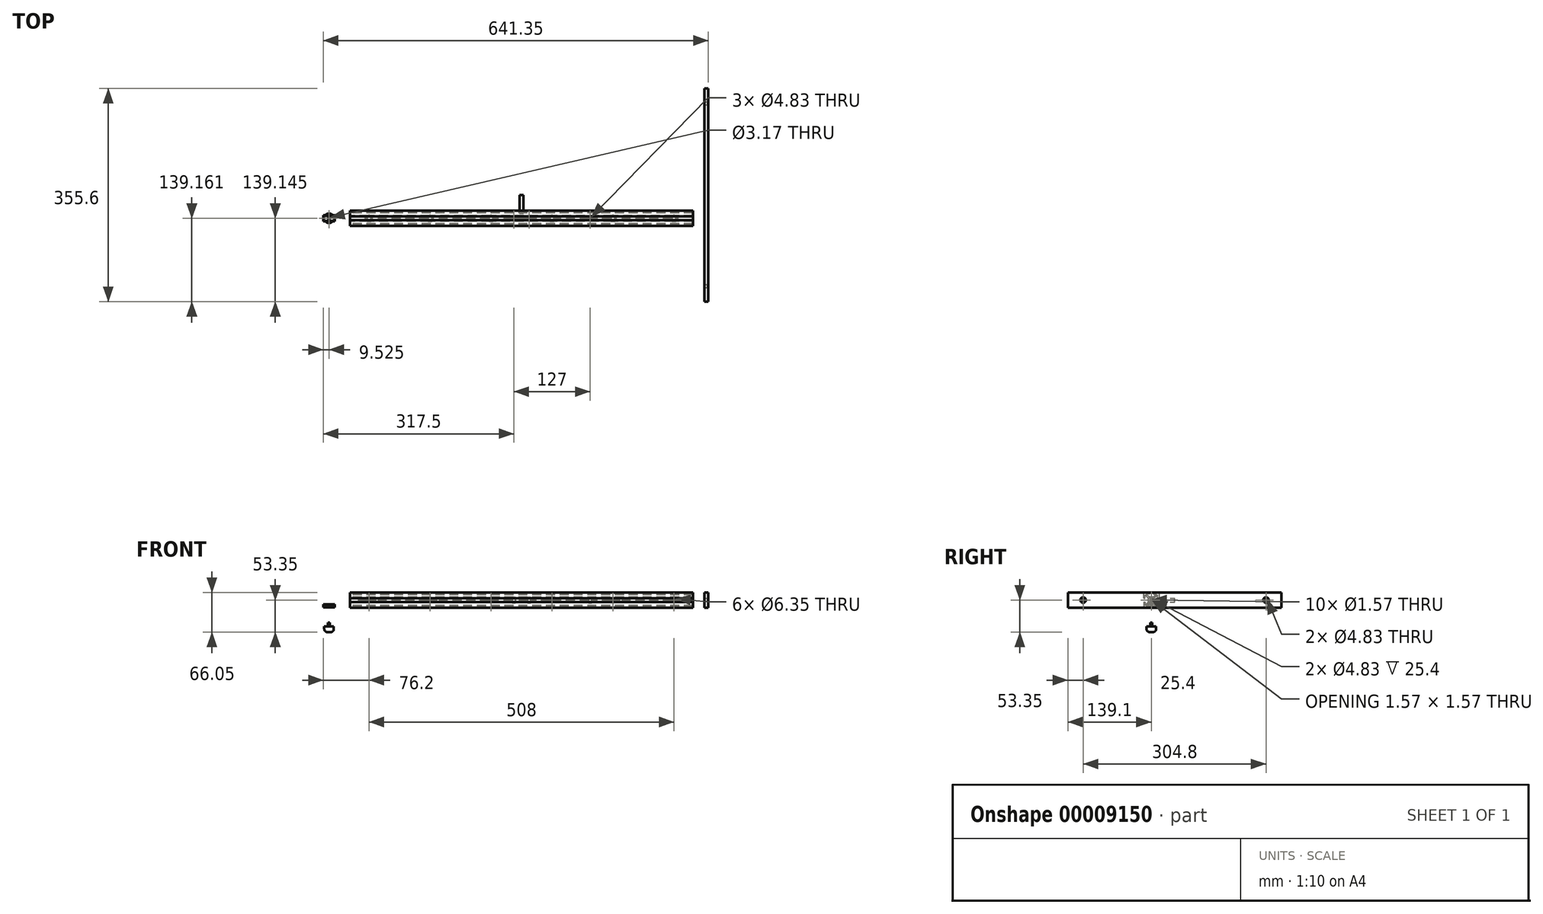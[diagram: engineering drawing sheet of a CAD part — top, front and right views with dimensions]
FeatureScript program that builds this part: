
annotation { "Feature Type Name" : "Feature", "Feature Type Description" : "" }
export const myFeature = defineFeature(function(context is Context, id is Id, definition is map)
    precondition{}
    {
        {
            var Q0;
            Q0=qCreatedBy(makeId("Right.planeOp"),FACE);
            var sketch = newSketch(context, id + "F0", { "sketchPlane" : qUnion([Q0])});
            skLineSegment(sketch, "E0.rect.bottom", {"start": v(-26, -12.7) * mm, "end": v(-35.53, -12.7) * mm});
            skLineSegment(sketch, "E0.rect.left", {"start": v(-26, -12.7) * mm, "end": v(-26, -3.18) * mm});
            skPoint(sketch, "E0.rect.middle", {"position": v(-38.7, 0) * mm});
            skLineSegment(sketch, "E1", {"start": v(-41.88, 12.7) * mm, "end": v(-41.88, 10.34) * mm});
            skLineSegment(sketch, "E2", {"start": v(-51.4, 3.17) * mm, "end": v(-49.04, 3.17) * mm});
            skLineSegment(sketch, "E3.rect.bottom", {"start": v(-35.6, -4.76) * mm, "end": v(-41.79, -4.76) * mm});
            skLineSegment(sketch, "E3.rect.top", {"start": v(-35.6, 4.76) * mm, "end": v(-41.8, 4.76) * mm});
            skLineSegment(sketch, "E3.rect.left", {"start": v(-33.94, -3.1) * mm, "end": v(-33.94, 3.1) * mm});
            skLineSegment(sketch, "E3.rect.right", {"start": v(-43.46, -3.09) * mm, "end": v(-43.46, 3.1) * mm});
            skLineSegment(sketch, "E4", {"start": v(-47.37, 10.34) * mm, "end": v(-41.8, 4.76) * mm});
            skLineSegment(sketch, "E5", {"start": v(-49.04, 8.67) * mm, "end": v(-43.46, 3.1) * mm});
            skLineSegment(sketch, "E6", {"start": v(-41.88, 10.34) * mm, "end": v(-47.37, 10.34) * mm});
            skLineSegment(sketch, "E7", {"start": v(-49.04, 3.17) * mm, "end": v(-49.04, 8.67) * mm});
            skLineSegment(sketch, "E8", {"start": v(-35.53, -12.7) * mm, "end": v(-35.53, -10.34) * mm});
            skLineSegment(sketch, "E9", {"start": v(-26, -3.18) * mm, "end": v(-28.36, -3.18) * mm});
            skLineSegment(sketch, "E10", {"start": v(-35.53, -10.34) * mm, "end": v(-30.03, -10.34) * mm});
            skLineSegment(sketch, "E11", {"start": v(-28.36, -3.18) * mm, "end": v(-28.36, -8.67) * mm});
            skLineSegment(sketch, "E12.trimOffspring", {"start": v(-35.6, -4.76) * mm, "end": v(-30.03, -10.34) * mm});
            skLineSegment(sketch, "E13.trimOffspring", {"start": v(-33.94, -3.1) * mm, "end": v(-28.36, -8.67) * mm});
            skLineSegment(sketch, "E14", {"start": v(-51.4, 12.7) * mm, "end": v(-41.88, 12.7) * mm});
            skLineSegment(sketch, "E15", {"start": v(-51.4, -3.18) * mm, "end": v(-49.04, -3.18) * mm});
            skLineSegment(sketch, "E16", {"start": v(-41.88, -12.7) * mm, "end": v(-41.88, -10.34) * mm});
            skLineSegment(sketch, "E17", {"start": v(-49.04, -3.18) * mm, "end": v(-49.04, -8.66) * mm});
            skLineSegment(sketch, "E18", {"start": v(-41.88, -10.34) * mm, "end": v(-47.36, -10.34) * mm});
            skLineSegment(sketch, "E19", {"start": v(-26, 3.17) * mm, "end": v(-28.36, 3.17) * mm});
            skLineSegment(sketch, "E20", {"start": v(-28.36, 3.17) * mm, "end": v(-28.36, 8.67) * mm});
            skLineSegment(sketch, "E21", {"start": v(-35.53, 12.7) * mm, "end": v(-35.53, 10.34) * mm});
            skLineSegment(sketch, "E22.trimOffspring", {"start": v(-41.88, 12.7) * mm, "end": v(-51.4, 12.7) * mm});
            skLineSegment(sketch, "E23.trimOffspring", {"start": v(-51.4, 3.17) * mm, "end": v(-51.4, 12.7) * mm});
            skLineSegment(sketch, "E24.trimOffspring", {"start": v(-43.46, -3.09) * mm, "end": v(-49.04, -8.66) * mm});
            skLineSegment(sketch, "E25.trimOffspring", {"start": v(-41.79, -4.76) * mm, "end": v(-47.36, -10.34) * mm});
            skLineSegment(sketch, "E26", {"start": v(-35.53, 12.7) * mm, "end": v(-26, 12.7) * mm});
            skLineSegment(sketch, "E27", {"start": v(-26, 12.7) * mm, "end": v(-26, 3.17) * mm});
            skLineSegment(sketch, "E28", {"start": v(-51.4, -3.18) * mm, "end": v(-51.4, -12.7) * mm});
            skLineSegment(sketch, "E29", {"start": v(-51.4, -12.7) * mm, "end": v(-41.88, -12.7) * mm});
            skCircle(sketch, "E30", {"center": v(-38.7, 0) * mm, "radius": 0.79 * mm});
            skLineSegment(sketch, "E31", {"start": v(-35.53, 10.34) * mm, "end": v(-30.03, 10.34) * mm});
            skLineSegment(sketch, "E32", {"start": v(-30.03, 10.34) * mm, "end": v(-35.6, 4.76) * mm});
            skLineSegment(sketch, "E33", {"start": v(-28.36, 8.67) * mm, "end": v(-33.94, 3.1) * mm});
            skSolve(sketch);
        }
        {
            var Q0;
            Q0=makeQuery(id+"F0.imprint","IMPRINT",FACE,{"disambiguationData":[TD([[makeQuery(id+"F0.imprint","IMPRINT",EDGE,{"derivedFrom":sQuery(id+"F0.wireOp",EDGE,"E0.rect.bottom")}),-1.0]])]});
            extrude(context, id + "F1", {"entities" : qUnion([Q0]), "depth" : 285.75 * mm, "hasSecondDirection" : true, "secondDirectionOppositeDirection" : true, "secondDirectionDepth" : 285.75 * mm});
        }
        {
            var Q0;
            Q0=makeQuery(id+"F1.opExtrude","SWEPT_FACE",FACE,{"disambiguationData":[OSD([sQuery(id+"F0.wireOp",EDGE,"E23.trimOffspring")])]});
            cPlane(context, id + "F2", {"entities" : qUnion([Q0]), "cplaneType" : CPlaneType.OFFSET, "offset" : 0 * mm, "width" : 152.4 * mm, "height" : 152.4 * mm});
        }
        {
            var Q0;
            Q0=qCreatedBy(id+"F2.planeOp",FACE);
            var sketch = newSketch(context, id + "F3", { "sketchPlane" : qUnion([Q0])});
            skCircle(sketch, "E34", {"center": v(-50.8, 0) * mm, "radius": 3.18 * mm});
            skCircle(sketch, "E35", {"center": v(50.8, 0) * mm, "radius": 3.18 * mm});
            skCircle(sketch, "E36", {"center": v(152.4, 0) * mm, "radius": 3.18 * mm});
            skCircle(sketch, "E37", {"center": v(254, 0) * mm, "radius": 3.18 * mm});
            skCircle(sketch, "E38", {"center": v(-254, 0) * mm, "radius": 3.18 * mm});
            skCircle(sketch, "E39", {"center": v(-152.4, 0) * mm, "radius": 3.18 * mm});
            skSolve(sketch);
        }
        {
            var Q0;
            Q0=makeQuery(id+"F3.imprint","IMPRINT",FACE,{"disambiguationData":[TD([[makeQuery(id+"F3.imprint","IMPRINT",EDGE,{"derivedFrom":sQuery(id+"F3.wireOp",EDGE,"9be4c3ad-e5e0-4c26-be88-867d9b3b50b8")}),1.0]])]});
            var Q1;
            Q1=makeQuery(id+"F3.imprint","IMPRINT",FACE,{"disambiguationData":[TD([[makeQuery(id+"F3.imprint","IMPRINT",EDGE,{"derivedFrom":sQuery(id+"F3.wireOp",EDGE,"E37")}),1.0]])]});
            var Q2;
            Q2=makeQuery(id+"F3.imprint","IMPRINT",FACE,{"disambiguationData":[TD([[makeQuery(id+"F3.imprint","IMPRINT",EDGE,{"derivedFrom":sQuery(id+"F3.wireOp",EDGE,"E36")}),1.0]])]});
            var Q3;
            Q3=makeQuery(id+"F3.imprint","IMPRINT",FACE,{"disambiguationData":[TD([[makeQuery(id+"F3.imprint","IMPRINT",EDGE,{"derivedFrom":sQuery(id+"F3.wireOp",EDGE,"E35")}),1.0]])]});
            var Q4;
            Q4=makeQuery(id+"F3.imprint","IMPRINT",FACE,{"disambiguationData":[TD([[makeQuery(id+"F3.imprint","IMPRINT",EDGE,{"derivedFrom":sQuery(id+"F3.wireOp",EDGE,"E34")}),1.0]])]});
            var Q5;
            Q5=makeQuery(id+"F3.imprint","IMPRINT",FACE,{"disambiguationData":[TD([[makeQuery(id+"F3.imprint","IMPRINT",EDGE,{"derivedFrom":sQuery(id+"F3.wireOp",EDGE,"E39")}),1.0]])]});
            var Q6;
            Q6=makeQuery(id+"F3.imprint","IMPRINT",FACE,{"disambiguationData":[TD([[makeQuery(id+"F3.imprint","IMPRINT",EDGE,{"derivedFrom":sQuery(id+"F3.wireOp",EDGE,"E38")}),1.0]])]});
            extrude(context, id + "F4", {"entities" : qUnion([Q0, Q1, Q2, Q3, Q4, Q5, Q6]), "operationType" : NewBodyOperationType.REMOVE, "endBound" : BoundingType.THROUGH_ALL, "oppositeDirection" : true, "depth" : 12.7 * mm});
        }
        {
            var Q0;
            Q0=qCreatedBy(makeId("Front.planeOp"),FACE);
            var sketch = newSketch(context, id + "F5", { "sketchPlane" : qUnion([Q0])});
            skCircle(sketch, "E40", {"center": v(0, 0) * mm, "radius": 3.18 * mm});
            skSolve(sketch);
        }
        {
            var Q0;
            Q0=makeQuery(id+"F5.imprint","IMPRINT",FACE,{"disambiguationData":[TD([[makeQuery(id+"F5.imprint","IMPRINT",EDGE,{"derivedFrom":sQuery(id+"F5.wireOp",EDGE,"E40")}),1.0]])]});
            extrude(context, id + "F6", {"entities" : qUnion([Q0]), "depth" : 30.15 * mm});
        }
        {
            var Q0;
            Q0=makeQuery(id+"F1.opExtrude","SWEPT_FACE",FACE,{"disambiguationData":[OSD([sQuery(id+"F0.wireOp",EDGE,"E29")])]});
            cPlane(context, id + "F7", {"entities" : qUnion([Q0]), "cplaneType" : CPlaneType.OFFSET, "offset" : 0 * mm, "width" : 152.4 * mm, "height" : 152.4 * mm});
        }
        {
            var Q0;
            Q0=qCreatedBy(id+"F7.planeOp",FACE);
            var sketch = newSketch(context, id + "F8", { "sketchPlane" : qUnion([Q0])});
            skPoint(sketch, "E41", {"position": v(114.3, 38.65) * mm});
            skLineSegment(sketch, "E42", {"start": v(114.3, 48.26) * mm, "end": v(114.3, 29.05) * mm, "construction": true});
            skCircle(sketch, "E43", {"center": v(114.3, 38.65) * mm, "radius": 2.41 * mm});
            skCircle(sketch, "E44", {"center": v(-12.7, 38.65) * mm, "radius": 2.41 * mm});
            skCircle(sketch, "E45", {"center": v(12.7, 38.65) * mm, "radius": 2.41 * mm});
            skSolve(sketch);
        }
        {
            var Q0;
            Q0=makeQuery(id+"F8.imprint","IMPRINT",FACE,{"disambiguationData":[TD([[makeQuery(id+"F8.imprint","IMPRINT",EDGE,{"derivedFrom":sQuery(id+"F8.wireOp",EDGE,"E43")}),1.0]])]});
            var Q1;
            Q1=makeQuery(id+"F8.imprint","IMPRINT",FACE,{"disambiguationData":[TD([[makeQuery(id+"F8.imprint","IMPRINT",EDGE,{"derivedFrom":sQuery(id+"F8.wireOp",EDGE,"E45")}),1.0]])]});
            var Q2;
            Q2=makeQuery(id+"F8.imprint","IMPRINT",FACE,{"disambiguationData":[TD([[makeQuery(id+"F8.imprint","IMPRINT",EDGE,{"derivedFrom":sQuery(id+"F8.wireOp",EDGE,"E44")}),1.0]])]});
            extrude(context, id + "F9", {"entities" : qUnion([Q0, Q1, Q2]), "operationType" : NewBodyOperationType.REMOVE, "endBound" : BoundingType.THROUGH_ALL, "oppositeDirection" : true, "depth" : 25.4 * mm});
        }
        {
            var Q0;
            Q0=makeQuery(id+"F1.opExtrude","CAP_FACE",FACE,{"disambiguationData":[OSD([sQuery(id+"F0.wireOp",EDGE,"E0.rect.bottom"),sQuery(id+"F0.wireOp",EDGE,"E1"),sQuery(id+"F0.wireOp",EDGE,"E2"),sQuery(id+"F0.wireOp",EDGE,"E3.rect.bottom"),sQuery(id+"F0.wireOp",EDGE,"E3.rect.top"),sQuery(id+"F0.wireOp",EDGE,"E3.rect.left"),sQuery(id+"F0.wireOp",EDGE,"E3.rect.right"),sQuery(id+"F0.wireOp",EDGE,"E4"),sQuery(id+"F0.wireOp",EDGE,"E5"),sQuery(id+"F0.wireOp",EDGE,"E6"),sQuery(id+"F0.wireOp",EDGE,"E7"),sQuery(id+"F0.wireOp",EDGE,"E8"),sQuery(id+"F0.wireOp",EDGE,"E9"),sQuery(id+"F0.wireOp",EDGE,"E10"),sQuery(id+"F0.wireOp",EDGE,"E11"),sQuery(id+"F0.wireOp",EDGE,"E12.trimOffspring"),sQuery(id+"F0.wireOp",EDGE,"E13.trimOffspring"),sQuery(id+"F0.wireOp",EDGE,"E0.rect.left"),sQuery(id+"F0.wireOp",EDGE,"E15"),sQuery(id+"F0.wireOp",EDGE,"E16"),sQuery(id+"F0.wireOp",EDGE,"E17"),sQuery(id+"F0.wireOp",EDGE,"E18"),sQuery(id+"F0.wireOp",EDGE,"E19"),sQuery(id+"F0.wireOp",EDGE,"E20"),sQuery(id+"F0.wireOp",EDGE,"E21"),sQuery(id+"F0.wireOp",EDGE,"E22.trimOffspring"),sQuery(id+"F0.wireOp",EDGE,"E23.trimOffspring"),sQuery(id+"F0.wireOp",EDGE,"E24.trimOffspring"),sQuery(id+"F0.wireOp",EDGE,"E25.trimOffspring"),sQuery(id+"F0.wireOp",EDGE,"E26"),sQuery(id+"F0.wireOp",EDGE,"E27"),sQuery(id+"F0.wireOp",EDGE,"E28"),sQuery(id+"F0.wireOp",EDGE,"E29"),sQuery(id+"F0.wireOp",EDGE,"E30"),sQuery(id+"F0.wireOp",EDGE,"E31"),sQuery(id+"F0.wireOp",EDGE,"E32"),sQuery(id+"F0.wireOp",EDGE,"E33")])],"isStart":false});
            var sketch = newSketch(context, id + "F10", { "sketchPlane" : qUnion([Q0])});
            skCircle(sketch, "E46", {"center": v(-38.7, 0) * mm, "radius": 2.41 * mm});
            skSolve(sketch);
        }
        {
            var Q0;
            Q0=makeQuery(id+"F10.imprint","IMPRINT",FACE,{"disambiguationData":[TD([[makeQuery(id+"F10.imprint","IMPRINT",EDGE,{"derivedFrom":sQuery(id+"F10.wireOp",EDGE,"E46")}),1.0]])]});
            extrude(context, id + "F11", {"entities" : qUnion([Q0]), "operationType" : NewBodyOperationType.REMOVE, "oppositeDirection" : true, "depth" : 25.4 * mm});
        }
        {
            var Q0;
            Q0=makeQuery(id+"F1.opExtrude","CAP_FACE",FACE,{"disambiguationData":[OSD([sQuery(id+"F0.wireOp",EDGE,"E0.rect.bottom"),sQuery(id+"F0.wireOp",EDGE,"E1"),sQuery(id+"F0.wireOp",EDGE,"E2"),sQuery(id+"F0.wireOp",EDGE,"E3.rect.bottom"),sQuery(id+"F0.wireOp",EDGE,"E3.rect.top"),sQuery(id+"F0.wireOp",EDGE,"E3.rect.left"),sQuery(id+"F0.wireOp",EDGE,"E3.rect.right"),sQuery(id+"F0.wireOp",EDGE,"E4"),sQuery(id+"F0.wireOp",EDGE,"E5"),sQuery(id+"F0.wireOp",EDGE,"E6"),sQuery(id+"F0.wireOp",EDGE,"E7"),sQuery(id+"F0.wireOp",EDGE,"E8"),sQuery(id+"F0.wireOp",EDGE,"E9"),sQuery(id+"F0.wireOp",EDGE,"E10"),sQuery(id+"F0.wireOp",EDGE,"E11"),sQuery(id+"F0.wireOp",EDGE,"E12.trimOffspring"),sQuery(id+"F0.wireOp",EDGE,"E13.trimOffspring"),sQuery(id+"F0.wireOp",EDGE,"E0.rect.left"),sQuery(id+"F0.wireOp",EDGE,"E15"),sQuery(id+"F0.wireOp",EDGE,"E16"),sQuery(id+"F0.wireOp",EDGE,"E17"),sQuery(id+"F0.wireOp",EDGE,"E18"),sQuery(id+"F0.wireOp",EDGE,"E19"),sQuery(id+"F0.wireOp",EDGE,"E20"),sQuery(id+"F0.wireOp",EDGE,"E21"),sQuery(id+"F0.wireOp",EDGE,"E22.trimOffspring"),sQuery(id+"F0.wireOp",EDGE,"E23.trimOffspring"),sQuery(id+"F0.wireOp",EDGE,"E24.trimOffspring"),sQuery(id+"F0.wireOp",EDGE,"E25.trimOffspring"),sQuery(id+"F0.wireOp",EDGE,"E26"),sQuery(id+"F0.wireOp",EDGE,"E27"),sQuery(id+"F0.wireOp",EDGE,"E28"),sQuery(id+"F0.wireOp",EDGE,"E29"),sQuery(id+"F0.wireOp",EDGE,"E30"),sQuery(id+"F0.wireOp",EDGE,"E31"),sQuery(id+"F0.wireOp",EDGE,"E32"),sQuery(id+"F0.wireOp",EDGE,"E33")])],"isStart":true});
            var sketch = newSketch(context, id + "F12", { "sketchPlane" : qUnion([Q0])});
            skCircle(sketch, "E47", {"center": v(38.7, 0) * mm, "radius": 2.41 * mm});
            skSolve(sketch);
        }
        {
            var Q0;
            Q0=makeQuery(id+"F12.imprint","IMPRINT",FACE,{"disambiguationData":[TD([[makeQuery(id+"F12.imprint","IMPRINT",EDGE,{"derivedFrom":sQuery(id+"F12.wireOp",EDGE,"E47")}),1.0]])]});
            extrude(context, id + "F13", {"entities" : qUnion([Q0]), "operationType" : NewBodyOperationType.REMOVE, "oppositeDirection" : true, "depth" : 25.4 * mm});
        }
        {
            var Q0;
            Q0=qCreatedBy(makeId("Right.planeOp"),FACE);
            cPlane(context, id + "F14", {"entities" : qUnion([Q0]), "cplaneType" : CPlaneType.OFFSET, "offset" : 304.8 * mm, "width" : 152.4 * mm, "height" : 152.4 * mm});
        }
        {
            var Q0;
            Q0=qCreatedBy(id+"F14.planeOp",FACE);
            var sketch = newSketch(context, id + "F15", { "sketchPlane" : qUnion([Q0])});
            skLineSegment(sketch, "E48.rect.bottom", {"start": v(177.8, -12.7) * mm, "end": v(-177.8, -12.7) * mm});
            skLineSegment(sketch, "E48.rect.top", {"start": v(177.8, 12.7) * mm, "end": v(-177.8, 12.7) * mm});
            skLineSegment(sketch, "E48.rect.left", {"start": v(177.8, -12.7) * mm, "end": v(177.8, 12.7) * mm});
            skLineSegment(sketch, "E48.rect.right", {"start": v(-177.8, -12.7) * mm, "end": v(-177.8, 12.7) * mm});
            skPoint(sketch, "E48.rect.middle", {"position": v(0, 0) * mm});
            skCircle(sketch, "E49", {"center": v(-152.4, 0) * mm, "radius": 2.41 * mm});
            skCircle(sketch, "E50", {"center": v(152.4, 0) * mm, "radius": 2.41 * mm});
            skSolve(sketch);
        }
        {
            var Q0;
            Q0=makeQuery(id+"F15.imprint","IMPRINT",FACE,{"disambiguationData":[TD([[makeQuery(id+"F15.imprint","IMPRINT",EDGE,{"derivedFrom":sQuery(id+"F15.wireOp",EDGE,"E48.rect.bottom")}),-1.0]])]});
            extrude(context, id + "F16", {"entities" : qUnion([Q0]), "depth" : 6.35 * mm});
        }
        {
            var Q0;
            Q0=makeQuery(id+"F16.opExtrude","CAP_EDGE",EDGE,{"disambiguationData":[OSD([sQuery(id+"F15.wireOp",EDGE,"E49")])],"isStart":false});
            var Q1;
            Q1=makeQuery(id+"F16.opExtrude","CAP_EDGE",EDGE,{"disambiguationData":[OSD([sQuery(id+"F15.wireOp",EDGE,"E50")])],"isStart":false});
            chamfer(context, id + "F17", {"entities" : qUnion([Q0, Q1]), "chamferType" : ChamferType.OFFSET_ANGLE, "width" : 1.27 * mm, "oppositeDirection" : false, "angle" : 60 * degree, "tangentPropagation" : true});
        }
        {
            var Q0;
            Q0=makeQuery(id+"F1.opExtrude","CAP_FACE",FACE,{"disambiguationData":[OSD([sQuery(id+"F0.wireOp",EDGE,"E0.rect.bottom"),sQuery(id+"F0.wireOp",EDGE,"E1"),sQuery(id+"F0.wireOp",EDGE,"E2"),sQuery(id+"F0.wireOp",EDGE,"E3.rect.bottom"),sQuery(id+"F0.wireOp",EDGE,"E3.rect.top"),sQuery(id+"F0.wireOp",EDGE,"E3.rect.left"),sQuery(id+"F0.wireOp",EDGE,"E3.rect.right"),sQuery(id+"F0.wireOp",EDGE,"E4"),sQuery(id+"F0.wireOp",EDGE,"E5"),sQuery(id+"F0.wireOp",EDGE,"E6"),sQuery(id+"F0.wireOp",EDGE,"E7"),sQuery(id+"F0.wireOp",EDGE,"E8"),sQuery(id+"F0.wireOp",EDGE,"E9"),sQuery(id+"F0.wireOp",EDGE,"E10"),sQuery(id+"F0.wireOp",EDGE,"E11"),sQuery(id+"F0.wireOp",EDGE,"E12.trimOffspring"),sQuery(id+"F0.wireOp",EDGE,"E13.trimOffspring"),sQuery(id+"F0.wireOp",EDGE,"E0.rect.left"),sQuery(id+"F0.wireOp",EDGE,"E15"),sQuery(id+"F0.wireOp",EDGE,"E16"),sQuery(id+"F0.wireOp",EDGE,"E17"),sQuery(id+"F0.wireOp",EDGE,"E18"),sQuery(id+"F0.wireOp",EDGE,"E19"),sQuery(id+"F0.wireOp",EDGE,"E20"),sQuery(id+"F0.wireOp",EDGE,"E21"),sQuery(id+"F0.wireOp",EDGE,"E22.trimOffspring"),sQuery(id+"F0.wireOp",EDGE,"E23.trimOffspring"),sQuery(id+"F0.wireOp",EDGE,"E24.trimOffspring"),sQuery(id+"F0.wireOp",EDGE,"E25.trimOffspring"),sQuery(id+"F0.wireOp",EDGE,"E26"),sQuery(id+"F0.wireOp",EDGE,"E27"),sQuery(id+"F0.wireOp",EDGE,"E28"),sQuery(id+"F0.wireOp",EDGE,"E29"),sQuery(id+"F0.wireOp",EDGE,"E30"),sQuery(id+"F0.wireOp",EDGE,"E31"),sQuery(id+"F0.wireOp",EDGE,"E32"),sQuery(id+"F0.wireOp",EDGE,"E33")])],"isStart":true});
            cPlane(context, id + "F18", {"entities" : qUnion([Q0]), "cplaneType" : CPlaneType.OFFSET, "offset" : 25.4 * mm, "width" : 152.4 * mm, "height" : 152.4 * mm});
        }
        {
            var Q0;
            Q0=qCreatedBy(id+"F18.planeOp",FACE);
            var sketch = newSketch(context, id + "F19", { "sketchPlane" : qUnion([Q0])});
            skLineSegment(sketch, "E51.bottom", {"start": v(33.56, -7) * mm, "end": v(43.72, -7) * mm});
            skLineSegment(sketch, "E51.top", {"start": v(33.56, -10.17) * mm, "end": v(35.46, -10.17) * mm});
            skLineSegment(sketch, "E51.left", {"start": v(33.56, -7) * mm, "end": v(33.56, -10.17) * mm});
            skLineSegment(sketch, "E51.right", {"start": v(43.72, -7) * mm, "end": v(43.72, -10.17) * mm});
            skLineSegment(sketch, "E52", {"start": v(35.46, -10.17) * mm, "end": v(35.46, -12.07) * mm});
            skLineSegment(sketch, "E53", {"start": v(35.46, -12.07) * mm, "end": v(41.81, -12.07) * mm});
            skLineSegment(sketch, "E54", {"start": v(41.81, -12.07) * mm, "end": v(41.81, -10.17) * mm});
            skLineSegment(sketch, "E55.trimOffspring", {"start": v(41.81, -10.17) * mm, "end": v(43.72, -10.17) * mm});
            skSolve(sketch);
        }
        {
            var Q0;
            Q0=makeQuery(id+"F19.imprint","IMPRINT",FACE,{"disambiguationData":[TD([[makeQuery(id+"F19.imprint","IMPRINT",EDGE,{"derivedFrom":sQuery(id+"F19.wireOp",EDGE,"E51.bottom")}),-1.0]])]});
            extrude(context, id + "F20", {"entities" : qUnion([Q0]), "depth" : 19.05 * mm});
        }
        {
            var Q0;
            Q0=makeQuery(id+"F20.opExtrude","SWEPT_EDGE",EDGE,{"disambiguationData":[OSD([sQuery(id+"F19.wireOp",EDGE,"E51.bottom"),sQuery(id+"F19.wireOp",EDGE,"E51.left")])]});
            var Q1;
            Q1=makeQuery(id+"F20.opExtrude","SWEPT_EDGE",EDGE,{"disambiguationData":[OSD([sQuery(id+"F19.wireOp",EDGE,"E51.bottom"),sQuery(id+"F19.wireOp",EDGE,"E51.right")])]});
            chamfer(context, id + "F21", {"entities" : qUnion([Q0, Q1]), "width" : 0.5 * mm, "tangentPropagation" : true});
        }
        {
            var Q0;
            Q0=makeQuery(id+"F20.opExtrude","SWEPT_FACE",FACE,{"disambiguationData":[OSD([sQuery(id+"F19.wireOp",EDGE,"E53")])]});
            var sketch = newSketch(context, id + "F22", { "sketchPlane" : qUnion([Q0])});
            skLineSegment(sketch, "E56", {"start": v(-330.2, 38.64) * mm, "end": v(-311.15, 38.64) * mm, "construction": true});
            skLineSegment(sketch, "E57", {"start": v(-320.68, 41.81) * mm, "end": v(-320.68, 35.46) * mm, "construction": true});
            skCircle(sketch, "E58", {"center": v(-320.68, 38.64) * mm, "radius": 1.59 * mm});
            skSolve(sketch);
        }
        {
            var Q0;
            Q0=makeQuery(id+"F22.imprint","IMPRINT",FACE,{"disambiguationData":[TD([[makeQuery(id+"F22.imprint","IMPRINT",EDGE,{"derivedFrom":sQuery(id+"F22.wireOp",EDGE,"E58")}),1.0]])]});
            extrude(context, id + "F23", {"entities" : qUnion([Q0]), "operationType" : NewBodyOperationType.REMOVE, "endBound" : BoundingType.THROUGH_ALL, "oppositeDirection" : true, "depth" : 25.4 * mm});
        }
        {
            var Q0;
            Q0=makeQuery(id+"F20.opExtrude","SWEPT_FACE",FACE,{"disambiguationData":[OSD([sQuery(id+"F19.wireOp",EDGE,"E53")])]});
            cPlane(context, id + "F24", {"entities" : qUnion([Q0]), "cplaneType" : CPlaneType.OFFSET, "offset" : 25.4 * mm, "width" : 152.4 * mm, "height" : 152.4 * mm});
        }
        {
            var Q0;
            Q0=qCreatedBy(id+"F24.planeOp",FACE);
            var sketch = newSketch(context, id + "F25", { "sketchPlane" : qUnion([Q0])});
            skCircle(sketch, "E59.0", {"center": v(-320.68, 38.64) * mm, "radius": 1.59 * mm});
            skSolve(sketch);
        }
        {
            var Q0;
            Q0=makeQuery(id+"F25.imprint","IMPRINT",FACE,{"disambiguationData":[TD([[makeQuery(id+"F25.imprint","IMPRINT",EDGE,{"derivedFrom":sQuery(id+"F25.wireOp",EDGE,"E59.0")}),1.0]])]});
            extrude(context, id + "F26", {"entities" : qUnion([Q0]), "depth" : 6.35 * mm});
        }
        {
            var Q0;
            Q0=makeQuery(id+"F26.opExtrude","CAP_FACE",FACE,{"disambiguationData":[OSD([sQuery(id+"F25.wireOp",EDGE,"E59.0")])],"isStart":false});
            var sketch = newSketch(context, id + "F27", { "sketchPlane" : qUnion([Q0])});
            skCircle(sketch, "E60.0", {"center": v(-320.68, 38.64) * mm, "radius": 1.59 * mm});
            skCircle(sketch, "E61", {"center": v(-320.68, 38.64) * mm, "radius": 7.94 * mm});
            skSolve(sketch);
        }
        {
            var Q0;
            Q0=makeQuery(id+"F27.imprint","IMPRINT",FACE,{"disambiguationData":[TD([[makeQuery(id+"F27.imprint","IMPRINT",EDGE,{"derivedFrom":sQuery(id+"F27.wireOp",EDGE,"E60.0")}),-1.0]])]});
            var Q1;
            Q1=makeQuery(id+"F27.imprint","IMPRINT",FACE,{"disambiguationData":[TD([[makeQuery(id+"F27.imprint","IMPRINT",EDGE,{"derivedFrom":sQuery(id+"F27.wireOp",EDGE,"E60.0")}),1.0]])]});
            extrude(context, id + "F28", {"entities" : qUnion([Q0, Q1]), "operationType" : NewBodyOperationType.ADD, "depth" : 9.52 * mm});
        }
        {
            var Q0;
            Q0=makeQuery(id+"F28.opExtrude","CAP_EDGE",EDGE,{"disambiguationData":[OSD([sQuery(id+"F27.wireOp",EDGE,"E61")])],"isStart":false});
            fillet(context, id + "F29", {"entities" : qUnion([Q0]), "radius" : 5.08 * mm, "tangentPropagation" : true, "allowEdgeOverflow" : false});
        }
    });
